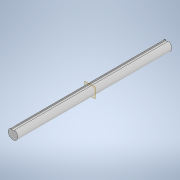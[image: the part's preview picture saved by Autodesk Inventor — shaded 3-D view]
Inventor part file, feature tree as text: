
AUTODESK INVENTOR PART (.ipt)
format: ipt  version: 2021.1 (Build 251245010, 245A)  size: 101,888 bytes
history: native  units: in
note: dims shown in document units (in); Inventor stores cm internally (conversion verified against a paired STEP export)
features: extrude x1, sketch x1
ambient origin geometry x8: Origin, YZ Plane, XZ Plane, XY Plane, X Axis, Y Axis, Z Axis, Center Point
bodies: Solid1 (feature_tree)
feature tree (2):
  extrude  "Extrusion1"  Depth=6.0in
  sketch  "Sketch1"  dims[d0=0.375in d1=0.0469in d2=0.0625in d3=6.0in d4=0.0in]
